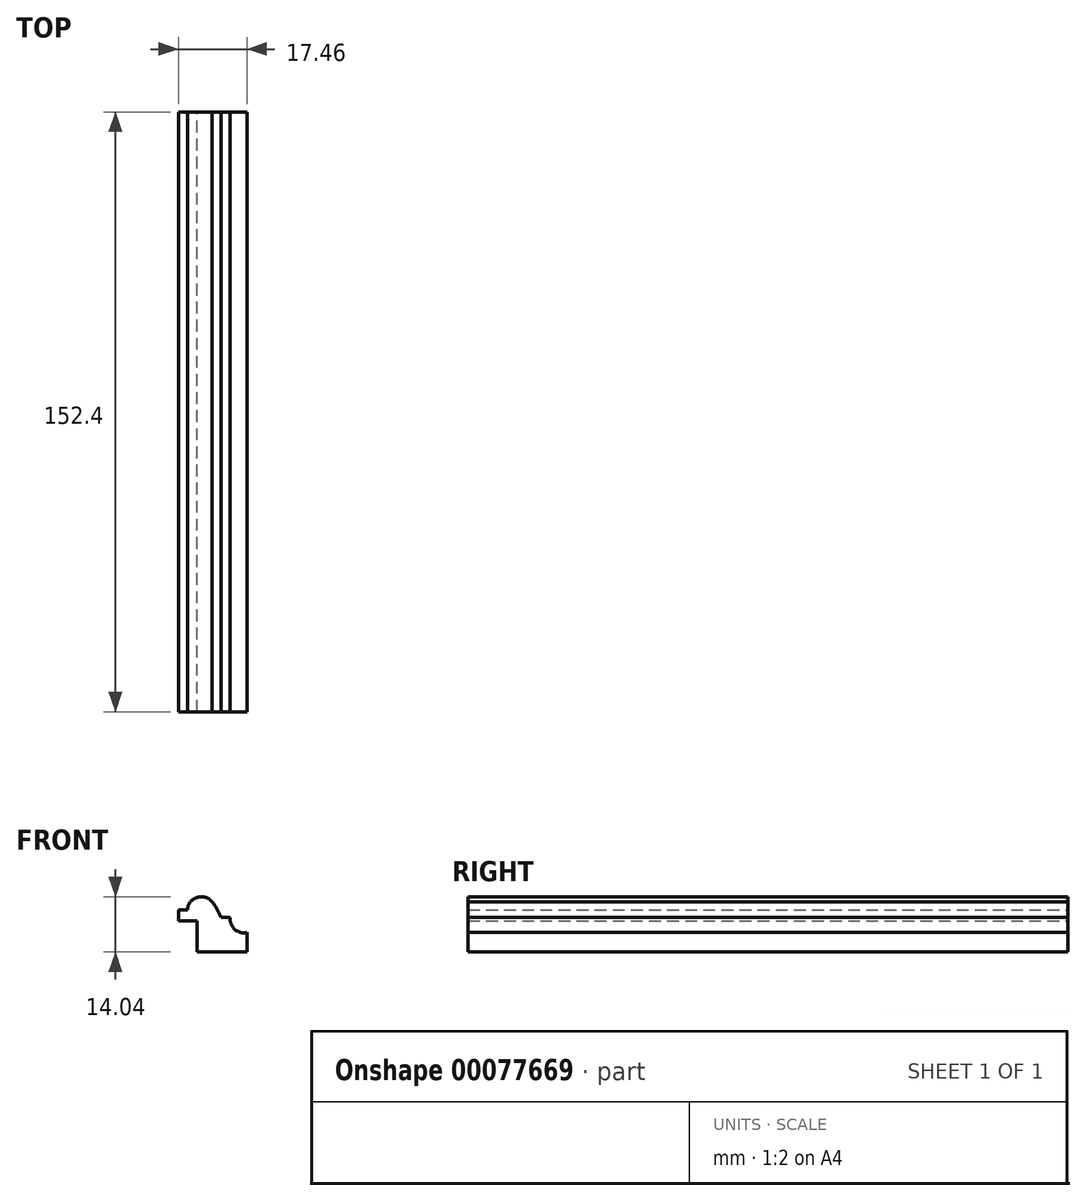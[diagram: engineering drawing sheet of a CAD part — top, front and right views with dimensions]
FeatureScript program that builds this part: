
annotation { "Feature Type Name" : "Feature", "Feature Type Description" : "" }
export const myFeature = defineFeature(function(context is Context, id is Id, definition is map)
    precondition{}
    {
        {
            var Q0;
            Q0=qCreatedBy(makeId("Front.planeOp"),FACE);
            var sketch = newSketch(context, id + "F0", { "sketchPlane" : qUnion([Q0])});
            skLineSegment(sketch, "E0", {"start": v(-8.73, 0.92) * mm, "end": v(-3.97, 0.92) * mm});
            skLineSegment(sketch, "E1", {"start": v(-3.97, -7.02) * mm, "end": v(-3.97, 0.92) * mm});
            skLineSegment(sketch, "E2", {"start": v(-3.97, -7.02) * mm, "end": v(8.73, -7.02) * mm});
            skLineSegment(sketch, "E3", {"start": v(8.73, -7.02) * mm, "end": v(8.73, -2.07) * mm});
            skLineSegment(sketch, "E4", {"start": v(-8.73, 3.71) * mm, "end": v(-8.73, 0.92) * mm});
            skLineSegment(sketch, "E5", {"start": v(-8.73, 3.71) * mm, "end": v(-6.45, 3.71) * mm});
            skLineSegment(sketch, "E6", {"start": v(2.06, 1.74) * mm, "end": v(4.18, 1.74) * mm});
            skArc(sketch, "E7", {"start": v(-0.2, 5.75) * mm, "mid": v(-4, 6.85) * mm, "end": v(-6.45, 3.71) * mm});
            skArc(sketch, "E8", {"start": v(2.06, 1.74) * mm, "mid": v(1.15, 3.87) * mm, "end": v(-0.2, 5.75) * mm});
            skArc(sketch, "E9", {"start": v(4.44, 1.48) * mm, "mid": v(5.7, -1.36) * mm, "end": v(8.73, -2.07) * mm});
            skArc(sketch, "E10", {"start": v(4.44, 1.48) * mm, "mid": v(4.37, 1.67) * mm, "end": v(4.18, 1.74) * mm});
            skSolve(sketch);
        }
        {
            var Q0;
            Q0=makeQuery(id+"F0.imprint","IMPRINT",FACE,{"disambiguationData":[TD([[makeQuery(id+"F0.imprint","IMPRINT",EDGE,{"derivedFrom":sQuery(id+"F0.wireOp",EDGE,"E2")}),1.0]])]});
            extrude(context, id + "F1", {"entities" : qUnion([Q0]), "depth" : 152.4 * mm});
        }
    });
